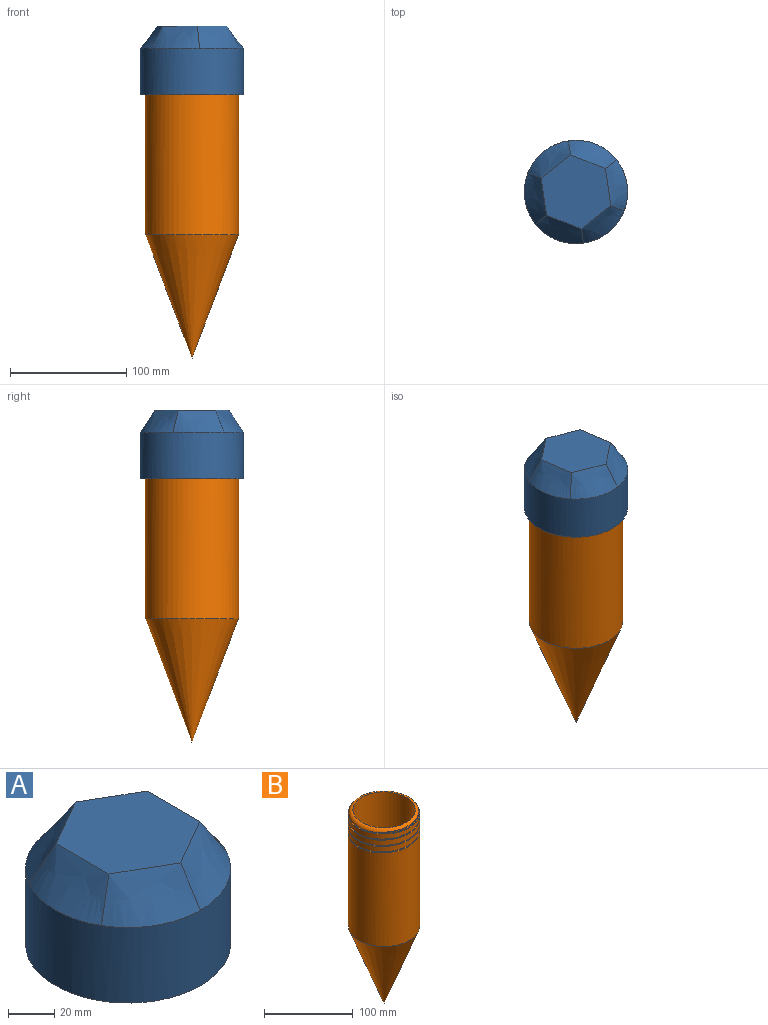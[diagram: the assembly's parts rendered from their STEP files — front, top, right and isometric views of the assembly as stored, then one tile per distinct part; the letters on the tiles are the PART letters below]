
ASSEMBLY  parts=2 mates=1
PART A: 18 faces, bbox 88.7x88.7x59 mm
  f0: cylinder r=35mm len=70mm, axis (0,0,-1), area 1916.3mm2, adj f3,f11,f12,f13,f15,f17
  f1: cylinder r=44.37mm len=88.75mm, axis (0,0,-1), area 11152.3mm2, adj f2,f5,f6,f7,f8,f9,f10
  f2: plane 88.75x88.75mm, normal (0,0,-1), area 1649.4mm2, adj f1,f11
  f3: plane 70x70mm, normal (0,0,-1), area 3848.5mm2, adj f0,f16
  f4: plane 64.41x55.78mm, normal (0,0,1), area 2694.3mm2, adj f5,f6,f7,f8,f9,f10
  f5: bspline ~44.37x19mm, area 943.9mm2, adj f1,f4,f6,f10
  f6: bspline ~38.43x28.27mm, area 943.9mm2, adj f1,f4,f5,f7
  f7: bspline ~38.43x28.27mm, area 943.9mm2, adj f1,f4,f6,f8
  f8: bspline ~44.37x19mm, area 943.9mm2, adj f1,f4,f7,f9
  f9: bspline ~38.43x28.27mm, area 943.9mm2, adj f1,f4,f8,f10
  f10: bspline ~38.43x28.27mm, area 943.9mm2, adj f1,f4,f5,f9
  f11: torus R=38mm, axis (0,0,1), area 939.6mm2, adj f0,f2,f12,f14,f15
  f12: plane 7.08x2mm, normal (0,1,0), area 12.6mm2, adj f0,f11,f14,f17
  f13: plane 7.25x2mm, normal (0,-1,0), area 14.5mm2, adj f0,f14,f15,f16,f17
  f14: cylinder r=37mm len=74mm, axis (0,0,1), area 6736.5mm2, adj f11,f12,f13,f15,f17
  f15: bspline ~74x74mm, area 1763.4mm2, adj f0,f11,f13,f14
  f16: cylinder r=35mm len=36.64mm, axis (0,0,1), area 63.7mm2, adj f3,f13,f17
  f17: bspline ~74x74mm, area 1811.6mm2, adj f0,f12,f13,f14,f16
PART B: 13 faces, bbox 86.6x86.6x266 mm
  f0: cylinder r=40mm len=132.25mm, axis (0,0,-1), area 32138.5mm2, adj f1,f7,f9,f10
  f1: cylinder r=40mm len=80mm, axis (0,0,-1), area 1822.2mm2, adj f0,f2,f10,f11
  f2: cylinder r=40mm len=80mm, axis (0,0,-1), area 1822.1mm2, adj f1,f3,f10,f11
  f3: cylinder r=40mm len=80mm, axis (0,0,-1), area 1646.6mm2, adj f2,f4,f8,f10,f11
  f4: cylinder r=40mm len=76.06mm, axis (0,0,-1), area 202.1mm2, adj f3,f8,f11
  f5: cylinder r=35mm len=150mm, axis (0,0,-1), area 32986.7mm2, adj f6,f8
  f6: plane 70x70mm, normal (0,0,1), area 3848.5mm2, adj f5
  f7: cone r=40mm half-angle=20.7deg, axis (0,0,1), area 14237.2mm2, adj f0
  f8: torus R=35mm, axis (0,0,1), area 1747.4mm2, adj f3,f4,f5,f10,f11,f12
  f9: plane 1.5x1mm, normal (0,1,0), area 1.5mm2, adj f0,f10,f11,f12
  f10: bspline ~80x80mm, area 936.1mm2, adj f0,f1,f2,f3,f8,f9,f12
  f11: bspline ~80x80mm, area 894mm2, adj f1,f2,f3,f4,f8,f9,f12
  f12: cylinder r=39mm len=78mm, axis (0,0,-1), area 1401.7mm2, adj f8,f9,f10,f11
PLACE A rot(axis=(0,0,1),8.4deg) t=(-77.05,-39.01,-49.53)mm
PLACE B t=(-77.05,-39.01,-9.53)mm fixed
MATE cylindrical B.f5 <-> A.f0  axis (0,0,1) through (-77.05,-39.01,140.47)mm
